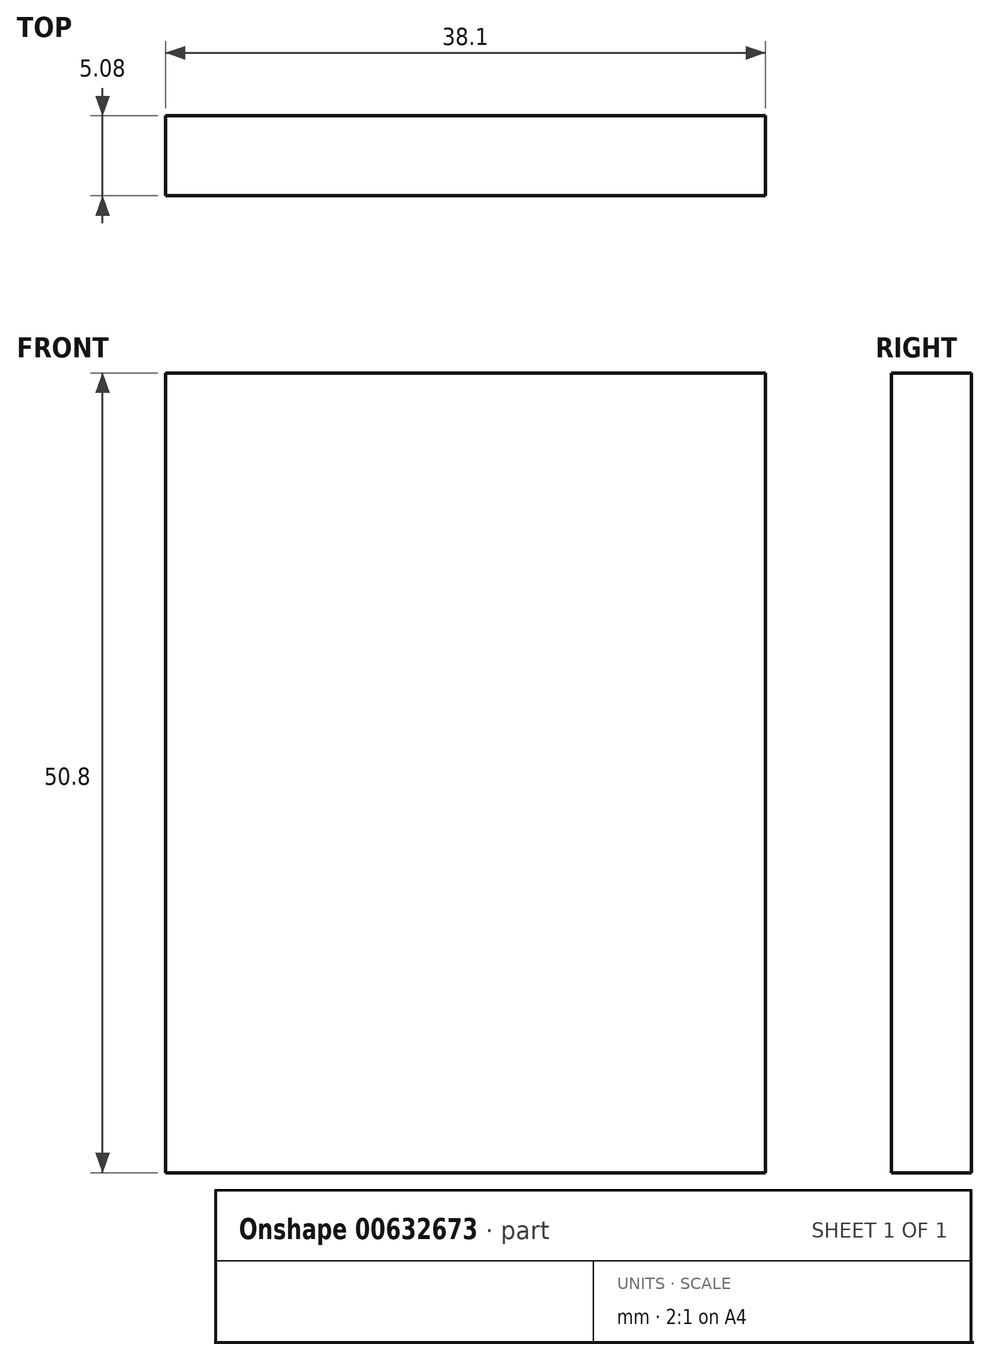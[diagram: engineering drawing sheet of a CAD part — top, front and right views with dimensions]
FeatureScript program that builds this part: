
annotation { "Feature Type Name" : "Feature", "Feature Type Description" : "" }
export const myFeature = defineFeature(function(context is Context, id is Id, definition is map)
    precondition{}
    {
        {
            var Q0;
            Q0=qCreatedBy(makeId("Front.planeOp"),FACE);
            var sketch = newSketch(context, id + "F0", { "sketchPlane" : qUnion([Q0])});
            skLineSegment(sketch, "E0.bottom", {"start": v(0, 0) * mm, "end": v(38.1, 0) * mm});
            skLineSegment(sketch, "E0.top", {"start": v(0, 50.8) * mm, "end": v(38.1, 50.8) * mm});
            skLineSegment(sketch, "E0.left", {"start": v(0, 0) * mm, "end": v(0, 50.8) * mm});
            skLineSegment(sketch, "E0.right", {"start": v(38.1, 0) * mm, "end": v(38.1, 50.8) * mm});
            skSolve(sketch);
        }
        {
            var Q0;
            Q0 = qSketchRegion(id + "F0", true);
            extrude(context, id + "F1", {"entities" : qUnion([Q0]), "depth" : 5.08 * mm, "offsetDistance" : 25.4 * mm});
        }
    });
